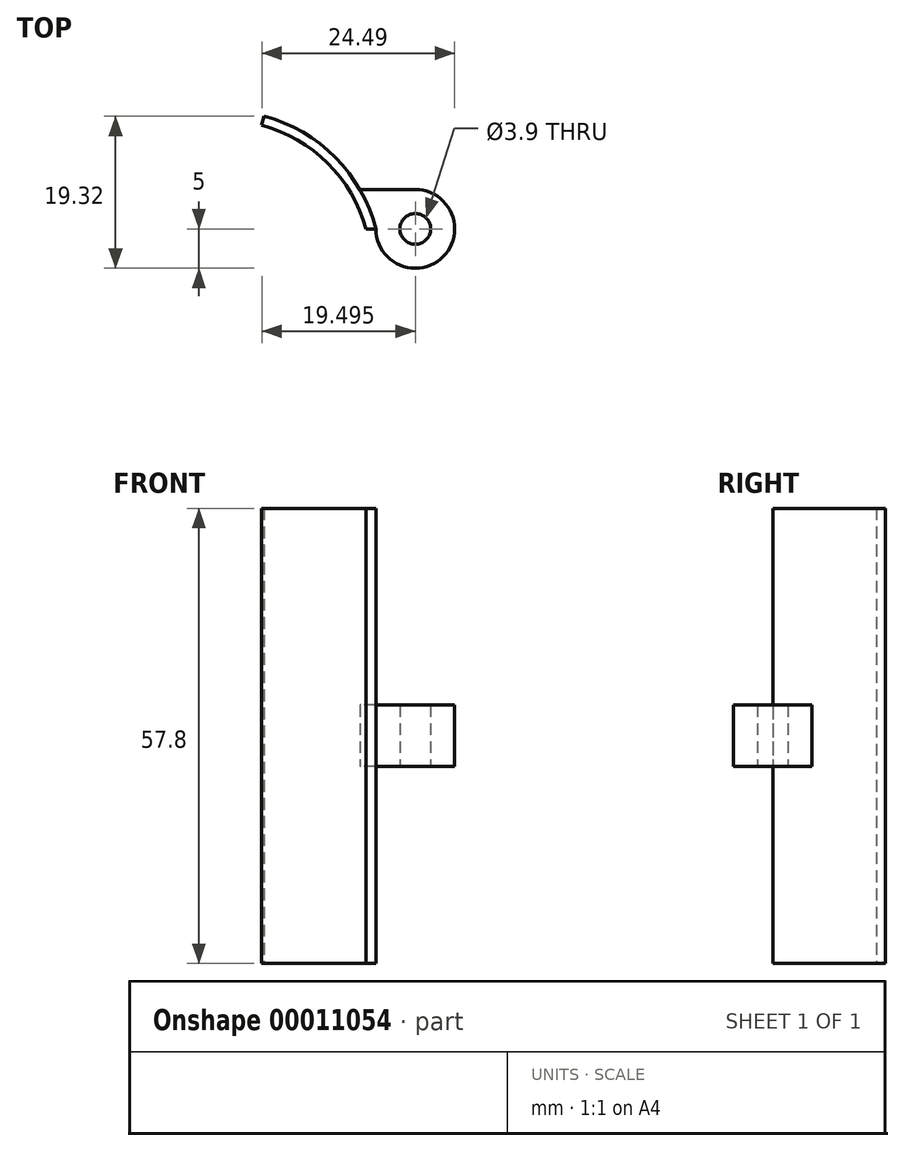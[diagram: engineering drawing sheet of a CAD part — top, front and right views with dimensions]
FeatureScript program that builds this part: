
annotation { "Feature Type Name" : "Feature", "Feature Type Description" : "" }
export const myFeature = defineFeature(function(context is Context, id is Id, definition is map)
    precondition{}
    {
        {
            var Q0;
            Q0=qCreatedBy(makeId("Top.planeOp"),FACE);
            var sketch = newSketch(context, id + "F0", { "sketchPlane" : qUnion([Q0])});
            skArc(sketch, "E0", {"start": v(17.3, 5) * mm, "mid": v(12.6, 12.85) * mm, "end": v(4.66, 17.39) * mm, "construction": true});
            skArc(sketch, "E1", {"start": v(19.36, 5) * mm, "mid": v(14.2, 14.08) * mm, "end": v(5.18, 19.32) * mm});
            skLineSegment(sketch, "E2", {"start": v(0, 0) * mm, "end": v(0, 20) * mm, "construction": true});
            skLineSegment(sketch, "E3", {"start": v(0, 0) * mm, "end": v(5.18, 19.32) * mm, "construction": true});
            skLineSegment(sketch, "E4", {"start": v(18.12, 5) * mm, "end": v(19.36, 5) * mm});
            skArc(sketch, "E5", {"start": v(18.12, 5) * mm, "mid": v(13.24, 13.34) * mm, "end": v(4.87, 18.16) * mm});
            skLineSegment(sketch, "E6", {"start": v(5.18, 19.32) * mm, "end": v(4.87, 18.16) * mm});
            skSolve(sketch);
        }
        {
            var Q0;
            Q0 = qSketchRegion(id + "F0", true);
            extrude(context, id + "F1", {"entities" : qUnion([Q0]), "depth" : 57.8 * mm});
        }
        {
            var Q0;
            Q0=makeQuery(id+"F1.opExtrude","CAP_FACE",FACE,{"disambiguationData":[OSD([sQuery(id+"F0.wireOp",EDGE,"E1"),sQuery(id+"F0.wireOp",EDGE,"E4"),sQuery(id+"F0.wireOp",EDGE,"E5"),sQuery(id+"F0.wireOp",EDGE,"E6")])],"isStart":false});
            cPlane(context, id + "F2", {"entities" : qUnion([Q0]), "cplaneType" : CPlaneType.OFFSET, "offset" : 28.9 * mm, "oppositeDirection" : true, "width" : 150 * mm, "height" : 150 * mm});
        }
        {
            var Q0;
            Q0=qCreatedBy(id+"F2.planeOp",FACE);
            var sketch = newSketch(context, id + "F3", { "sketchPlane" : qUnion([Q0])});
            skPoint(sketch, "E7.0", {"position": v(19.36, 5) * mm});
            skArc(sketch, "E8", {"start": v(19.36, 5) * mm, "mid": v(27.9, 1.46) * mm, "end": v(24.36, 10) * mm});
            skLineSegment(sketch, "E9", {"start": v(19.36, 3.02) * mm, "end": v(19.36, 7.49) * mm, "construction": true});
            skArc(sketch, "E10.0", {"start": v(19.36, 5) * mm, "mid": v(18.51, 7.57) * mm, "end": v(17.32, 10) * mm});
            skLineSegment(sketch, "E11", {"start": v(24.36, 10) * mm, "end": v(17.32, 10) * mm});
            skCircle(sketch, "E12", {"center": v(24.36, 5) * mm, "radius": 1.95 * mm});
            skPoint(sketch, "E13.orphan", {"position": v(5.18, 19.32) * mm});
            skSolve(sketch);
        }
        {
            var Q0;
            Q0 = qSketchRegion(id + "F3", true);
            extrude(context, id + "F4", {"entities" : qUnion([Q0]), "operationType" : NewBodyOperationType.ADD, "depth" : 3.9 * mm, "hasSecondDirection" : true, "secondDirectionOppositeDirection" : true, "secondDirectionDepth" : 3.9 * mm});
        }
    });
